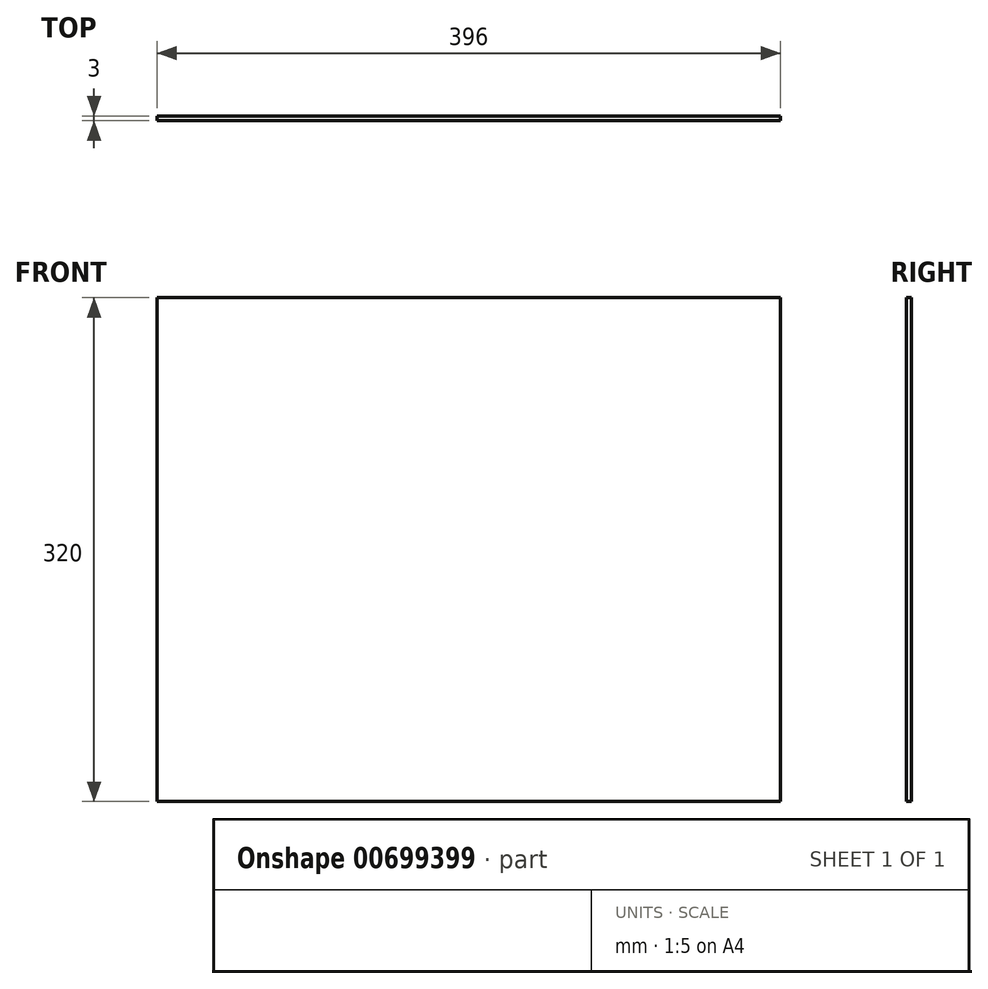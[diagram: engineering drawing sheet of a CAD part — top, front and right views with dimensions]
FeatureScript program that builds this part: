
annotation { "Feature Type Name" : "Feature", "Feature Type Description" : "" }
export const myFeature = defineFeature(function(context is Context, id is Id, definition is map)
    precondition{}
    {
        {
            var Q0;
            Q0=qCreatedBy(makeId("Front.planeOp"),FACE);
            var sketch = newSketch(context, id + "F0", { "sketchPlane" : qUnion([Q0])});
            skLineSegment(sketch, "E0", {"start": v(0, 0) * mm, "end": v(396, 0) * mm});
            skLineSegment(sketch, "E1", {"start": v(396, 0) * mm, "end": v(396, 320) * mm});
            skLineSegment(sketch, "E2", {"start": v(396, 320) * mm, "end": v(0, 320) * mm});
            skLineSegment(sketch, "E3", {"start": v(0, 320) * mm, "end": v(0, 0) * mm});
            skSolve(sketch);
        }
        {
            var Q0;
            Q0=makeQuery(id+"F0.imprint","IMPRINT",FACE,{"disambiguationData":[TD([[makeQuery(id+"F0.imprint","IMPRINT",EDGE,{"derivedFrom":sQuery(id+"F0.wireOp",EDGE,"E0")}),1.0]])]});
            extrude(context, id + "F1", {"entities" : qUnion([Q0]), "depth" : 3 * mm, "offsetDistance" : 25 * mm});
        }
    });
